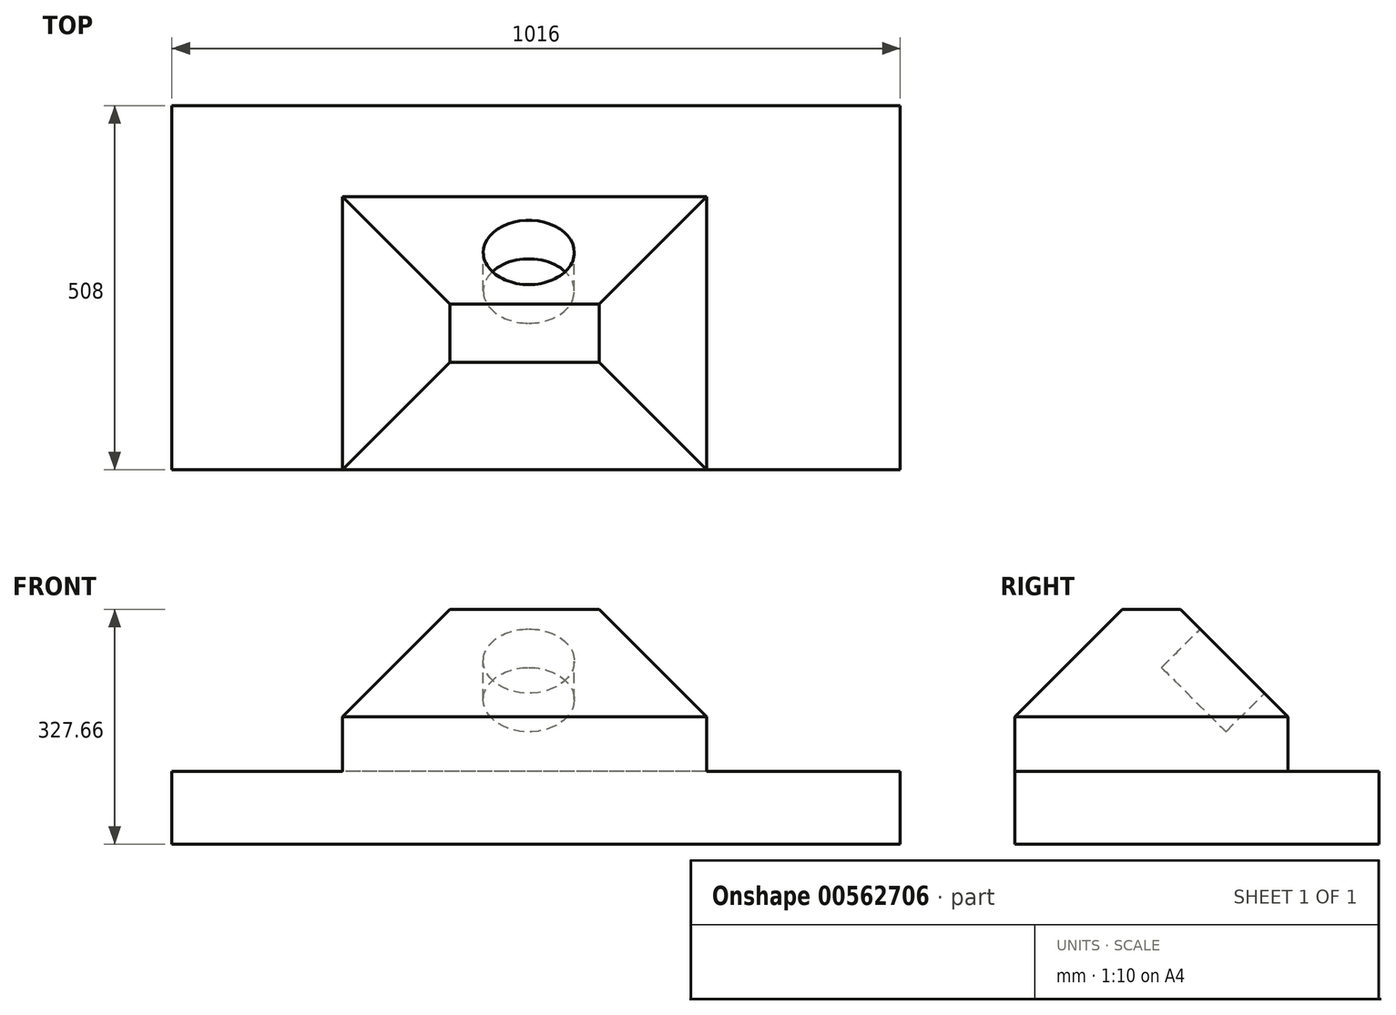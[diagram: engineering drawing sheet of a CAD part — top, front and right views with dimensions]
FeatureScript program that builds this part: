
annotation { "Feature Type Name" : "Feature", "Feature Type Description" : "" }
export const myFeature = defineFeature(function(context is Context, id is Id, definition is map)
    precondition{}
    {
        {
            var Q0;
            Q0=qCreatedBy(makeId("Top.planeOp"),FACE);
            var sketch = newSketch(context, id + "F0", { "sketchPlane" : qUnion([Q0])});
            skLineSegment(sketch, "E0.bottom", {"start": v(508, 254) * mm, "end": v(-508, 254) * mm});
            skLineSegment(sketch, "E0.top", {"start": v(508, -254) * mm, "end": v(-508, -254) * mm});
            skLineSegment(sketch, "E0.left", {"start": v(508, 254) * mm, "end": v(508, -254) * mm});
            skLineSegment(sketch, "E0.right", {"start": v(-508, 254) * mm, "end": v(-508, -254) * mm});
            skPoint(sketch, "E0.middle", {"position": v(0, 0) * mm});
            skSolve(sketch);
        }
        {
            var Q0;
            Q0 = qSketchRegion(id + "F0", true);
            extrude(context, id + "F1", {"entities" : qUnion([Q0]), "depth" : 101.6 * mm, "offsetDistance" : 25.4 * mm});
        }
        {
            var Q0;
            Q0=makeQuery(id+"F1.opExtrude","CAP_FACE",FACE,{"disambiguationData":[OSD([sQuery(id+"F0.wireOp",EDGE,"E0.bottom"),sQuery(id+"F0.wireOp",EDGE,"E0.top"),sQuery(id+"F0.wireOp",EDGE,"E0.left"),sQuery(id+"F0.wireOp",EDGE,"E0.right")])],"isStart":true});
            var sketch = newSketch(context, id + "F2", { "sketchPlane" : qUnion([Q0])});
            skCircle(sketch, "E1", {"center": v(-404.68, 181.33) * mm, "radius": 53.59 * mm});
            skPoint(sketch, "E1.first.point", {"position": v(-448.8, 211.74) * mm});
            skPoint(sketch, "E1.second.point", {"position": v(-391.29, 129.44) * mm});
            skPoint(sketch, "E1.third.point", {"position": v(-355.59, 202.82) * mm});
            skCircle(sketch, "E2.MirrorC", {"center": v(404.68, 181.33) * mm, "radius": 53.59 * mm});
            skCircle(sketch, "E3.MirrorC", {"center": v(-404.68, -181.33) * mm, "radius": 53.59 * mm});
            skCircle(sketch, "E4.MirrorC", {"center": v(404.68, -181.33) * mm, "radius": 53.59 * mm});
            skSolve(sketch);
        }
        {
            var Q0;
            Q0=sQuery(id+"F2.wireOp",EDGE,"E1");
            var Q1;
            Q1=sQuery(id+"F2.wireOp",EDGE,"E3.MirrorC");
            var Q2;
            Q2=sQuery(id+"F2.wireOp",EDGE,"E2.MirrorC");
            var Q3;
            Q3=sQuery(id+"F2.wireOp",EDGE,"E4.MirrorC");
            extrude(context, id + "F3", {"bodyType" : ToolBodyType.SURFACE, "surfaceEntities" : qUnion([Q0, Q1, Q2, Q3]), "depth" : 762 * mm, "offsetDistance" : 25.4 * mm});
        }
        {
            var Q0;
            Q0=makeQuery(id+"F1.opExtrude","CAP_FACE",FACE,{"disambiguationData":[OSD([sQuery(id+"F0.wireOp",EDGE,"E0.bottom"),sQuery(id+"F0.wireOp",EDGE,"E0.top"),sQuery(id+"F0.wireOp",EDGE,"E0.left"),sQuery(id+"F0.wireOp",EDGE,"E0.right")])],"isStart":false});
            var sketch = newSketch(context, id + "F4", { "sketchPlane" : qUnion([Q0])});
            skLineSegment(sketch, "E5", {"start": v(0, -254) * mm, "end": v(0, 254) * mm});
            skLineSegment(sketch, "E6", {"start": v(237.95, -254) * mm, "end": v(237.95, 127) * mm});
            skLineSegment(sketch, "E7", {"start": v(237.95, 127) * mm, "end": v(-270.05, 127) * mm});
            skLineSegment(sketch, "E8", {"start": v(-270.05, 127) * mm, "end": v(-270.05, -254) * mm});
            skSolve(sketch);
        }
        {
            var Q0;
            {var subQ5=sQuery(id+"F4.wireOp",EDGE,"E6");Q0=makeQuery(id+"F4.imprint","IMPRINT",FACE,{"disambiguationData":[TD([[makeQuery(id+"F4.imprint","IMPRINT",EDGE,{"derivedFrom":subQ5}),1.0]])]});}
            var Q1;
            {var subQ5=sQuery(id+"F4.wireOp",EDGE,"E8");Q1=makeQuery(id+"F4.imprint","IMPRINT",FACE,{"disambiguationData":[TD([[makeQuery(id+"F4.imprint","IMPRINT",EDGE,{"derivedFrom":subQ5}),1.0]])]});}
            extrude(context, id + "F5", {"entities" : qUnion([Q0, Q1]), "operationType" : NewBodyOperationType.ADD, "depth" : 76.2 * mm, "offsetDistance" : 25.4 * mm});
        }
        {
            var Q0;
            Q0=makeQuery(id+"F5.opExtrude","CAP_FACE",FACE,{"disambiguationData":[OSD([sQuery(id+"F0.wireOp",EDGE,"E0.top"),sQuery(id+"F4.wireOp",EDGE,"E6"),sQuery(id+"F4.wireOp",EDGE,"E7"),sQuery(id+"F4.wireOp",EDGE,"E8")])],"isStart":false});
            extrude(context, id + "F6", {"entities" : qUnion([Q0]), "operationType" : NewBodyOperationType.ADD, "endBound" : BoundingType.SYMMETRIC, "depth" : 299.72 * mm, "offsetDistance" : 25.4 * mm, "hasDraft" : true, "draftAngle" : 45 * degree, "draftPullDirection" : true});
        }
        {
            var Q0;
            Q0=makeQuery(id+"F6.*.split.splitOp","SPLIT",FACE,{"derivedFrom":makeQuery(id+"F6.opExtrude","SWEPT_FACE",FACE,{"disambiguationData":[OSD([sQuery(id+"F4.wireOp",EDGE,"E7")])]})});
            var sketch = newSketch(context, id + "F7", { "sketchPlane" : qUnion([Q0])});
            skCircle(sketch, "E9", {"center": v(10.23, 145.94) * mm, "radius": 63.5 * mm});
            skPoint(sketch, "E9.first.point", {"position": v(-43.76, 179.37) * mm});
            skPoint(sketch, "E9.second.point", {"position": v(47.3, 94.39) * mm});
            skPoint(sketch, "E9.third.point", {"position": v(62.11, 182.55) * mm});
            skSolve(sketch);
        }
        {
            var Q0;
            Q0 = qSketchRegion(id + "F7", true);
            extrude(context, id + "F8", {"entities" : qUnion([Q0]), "operationType" : NewBodyOperationType.REMOVE, "oppositeDirection" : true, "depth" : 76.2 * mm, "offsetDistance" : 25.4 * mm});
        }
    });
